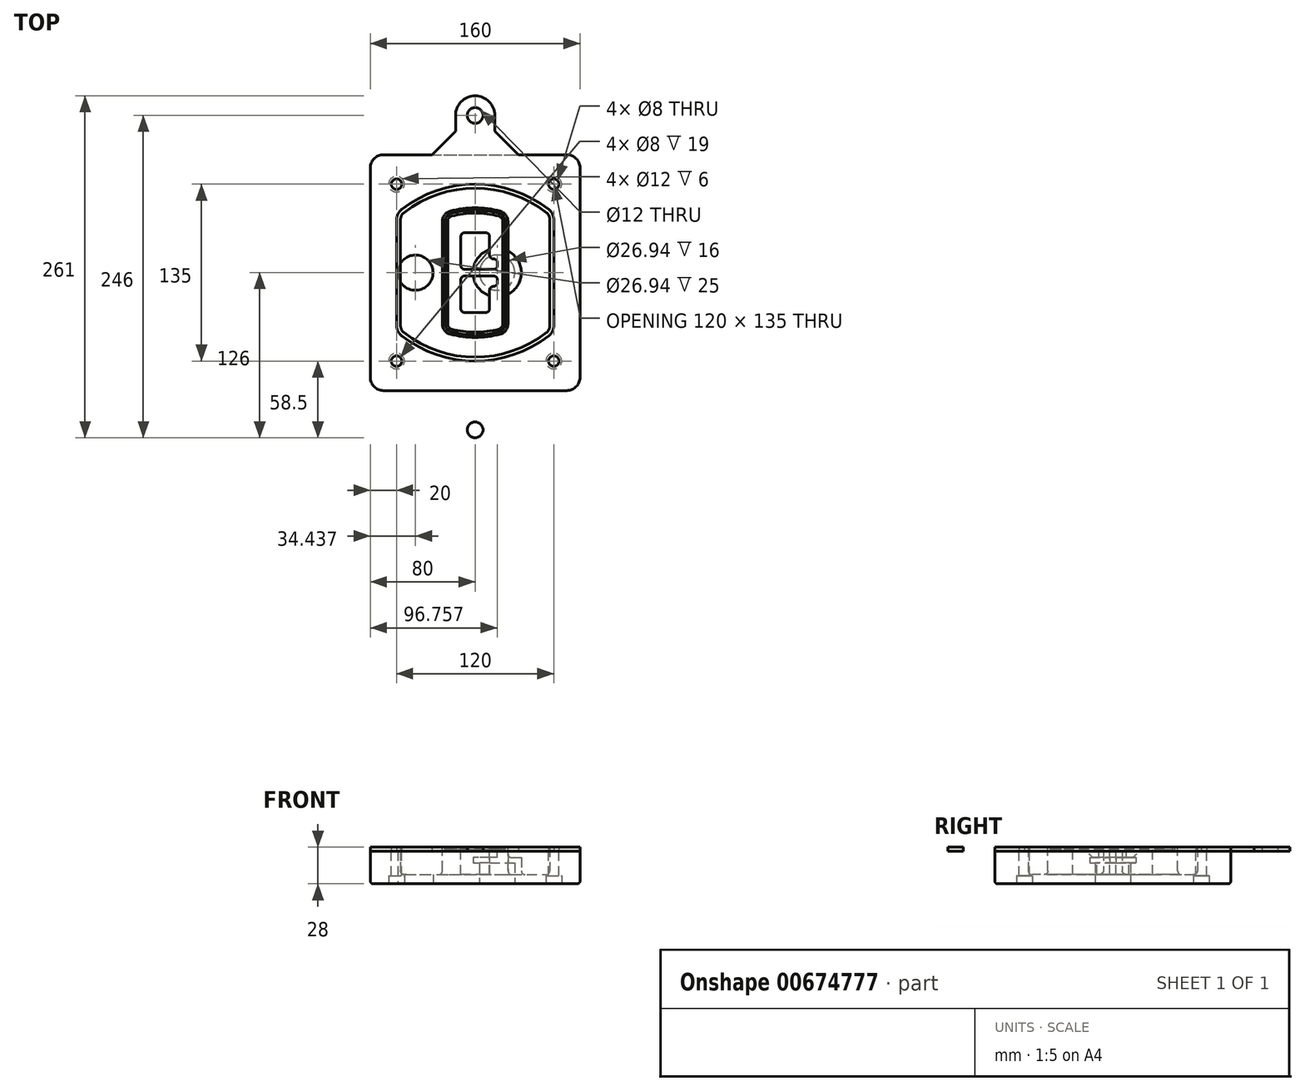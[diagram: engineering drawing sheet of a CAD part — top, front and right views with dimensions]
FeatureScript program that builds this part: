
annotation { "Feature Type Name" : "Feature", "Feature Type Description" : "" }
export const myFeature = defineFeature(function(context is Context, id is Id, definition is map)
    precondition{}
    {
        {
            var Q0;
            Q0=qCreatedBy(makeId("Top.planeOp"),FACE);
            var sketch = newSketch(context, id + "F0", { "sketchPlane" : qUnion([Q0])});
            skPoint(sketch, "E0.rect.middle", {"position": v(0, 0) * mm});
            skLineSegment(sketch, "E1.bottom", {"start": v(-70, -90) * mm, "end": v(70, -90) * mm});
            skLineSegment(sketch, "E1.top", {"start": v(-70, 90) * mm, "end": v(70, 90) * mm});
            skLineSegment(sketch, "E1.left", {"start": v(-80, -80) * mm, "end": v(-80, 80) * mm});
            skLineSegment(sketch, "E1.right", {"start": v(80, -80) * mm, "end": v(80, 80) * mm});
            skLineSegment(sketch, "E2", {"start": v(-80, 90) * mm, "end": v(80, -90) * mm, "construction": true});
            skLineSegment(sketch, "E3", {"start": v(80, 90) * mm, "end": v(-80, -90) * mm, "construction": true});
            skCircle(sketch, "E4", {"center": v(-60, 67.5) * mm, "radius": 4 * mm});
            skCircle(sketch, "E5", {"center": v(60, 67.5) * mm, "radius": 4 * mm});
            skCircle(sketch, "E6", {"center": v(60, -67.5) * mm, "radius": 4 * mm});
            skCircle(sketch, "E7", {"center": v(-60, -67.5) * mm, "radius": 4 * mm});
            skLineSegment(sketch, "E8", {"start": v(-60, 67.5) * mm, "end": v(60, 67.5) * mm, "construction": true});
            skLineSegment(sketch, "E9", {"start": v(60, 67.5) * mm, "end": v(60, -67.5) * mm, "construction": true});
            skLineSegment(sketch, "E10", {"start": v(60, -67.5) * mm, "end": v(-60, -67.5) * mm, "construction": true});
            skLineSegment(sketch, "E11", {"start": v(-60, -67.5) * mm, "end": v(-60, 67.5) * mm, "construction": true});
            skLineSegment(sketch, "E12", {"start": v(-60, 40.3) * mm, "end": v(-60, -40.3) * mm});
            skLineSegment(sketch, "E13", {"start": v(60, 40.3) * mm, "end": v(60, -40.3) * mm});
            skArc(sketch, "E14", {"start": v(56.15, 48.18) * mm, "mid": v(0, 67.5) * mm, "end": v(-56.15, 48.18) * mm});
            skArc(sketch, "E15", {"start": v(-56.15, -48.18) * mm, "mid": v(0, -67.5) * mm, "end": v(56.15, -48.18) * mm});
            skLineSegment(sketch, "E16", {"start": v(-60, 0) * mm, "end": v(60, 0) * mm, "construction": true});
            skPoint(sketch, "E17.visualSharp", {"position": v(-60, -45) * mm});
            skArc(sketch, "E17.filletArc", {"start": v(-60, -40.3) * mm, "mid": v(-58.99, -44.68) * mm, "end": v(-56.15, -48.18) * mm});
            skPoint(sketch, "E18.visualSharp", {"position": v(-60, 45) * mm});
            skArc(sketch, "E18.filletArc", {"start": v(-56.15, 48.18) * mm, "mid": v(-58.99, 44.68) * mm, "end": v(-60, 40.3) * mm});
            skPoint(sketch, "E19.visualSharp", {"position": v(60, 45) * mm});
            skArc(sketch, "E19.filletArc", {"start": v(60, 40.3) * mm, "mid": v(58.99, 44.68) * mm, "end": v(56.15, 48.18) * mm});
            skPoint(sketch, "E20.visualSharp", {"position": v(60, -45) * mm});
            skArc(sketch, "E20.filletArc", {"start": v(56.15, -48.18) * mm, "mid": v(58.99, -44.68) * mm, "end": v(60, -40.3) * mm});
            skPoint(sketch, "E21.visualSharp", {"position": v(-80, 90) * mm});
            skArc(sketch, "E21.filletArc", {"start": v(-70, 90) * mm, "mid": v(-77.07, 87.07) * mm, "end": v(-80, 80) * mm});
            skPoint(sketch, "E22.visualSharp", {"position": v(80, 90) * mm});
            skArc(sketch, "E22.filletArc", {"start": v(80, 80) * mm, "mid": v(77.07, 87.07) * mm, "end": v(70, 90) * mm});
            skPoint(sketch, "E23.visualSharp", {"position": v(80, -90) * mm});
            skArc(sketch, "E23.filletArc", {"start": v(70, -90) * mm, "mid": v(77.07, -87.07) * mm, "end": v(80, -80) * mm});
            skPoint(sketch, "E24.visualSharp", {"position": v(-80, -90) * mm});
            skArc(sketch, "E24.filletArc", {"start": v(-80, -80) * mm, "mid": v(-77.07, -87.07) * mm, "end": v(-70, -90) * mm});
            skArc(sketch, "E25.0", {"start": v(57, 40.3) * mm, "mid": v(56.3, 43.36) * mm, "end": v(54.3, 45.81) * mm});
            skLineSegment(sketch, "E25.1", {"start": v(57, 40.3) * mm, "end": v(57, -40.3) * mm});
            skArc(sketch, "E25.2", {"start": v(54.3, -45.81) * mm, "mid": v(56.3, -43.36) * mm, "end": v(57, -40.3) * mm});
            skArc(sketch, "E25.3", {"start": v(-54.3, -45.81) * mm, "mid": v(0, -64.5) * mm, "end": v(54.3, -45.81) * mm});
            skArc(sketch, "E25.4", {"start": v(-57, -40.3) * mm, "mid": v(-56.3, -43.36) * mm, "end": v(-54.3, -45.81) * mm});
            skArc(sketch, "E25.5", {"start": v(54.3, 45.81) * mm, "mid": v(0, 64.5) * mm, "end": v(-54.3, 45.81) * mm});
            skLineSegment(sketch, "E25.6", {"start": v(-57, 40.3) * mm, "end": v(-57, -40.3) * mm});
            skArc(sketch, "E25.7", {"start": v(-54.3, 45.81) * mm, "mid": v(-56.3, 43.36) * mm, "end": v(-57, 40.3) * mm});
            skArc(sketch, "E26.0", {"start": v(-58.62, 51.33) * mm, "mid": v(-62.58, 46.43) * mm, "end": v(-64, 40.3) * mm});
            skArc(sketch, "E26.1", {"start": v(58.62, 51.33) * mm, "mid": v(0, 71.5) * mm, "end": v(-58.62, 51.33) * mm});
            skArc(sketch, "E26.2", {"start": v(64, 40.3) * mm, "mid": v(62.58, 46.43) * mm, "end": v(58.62, 51.33) * mm});
            skLineSegment(sketch, "E26.3", {"start": v(64, 40.3) * mm, "end": v(64, -40.3) * mm});
            skArc(sketch, "E26.4", {"start": v(58.62, -51.33) * mm, "mid": v(62.58, -46.43) * mm, "end": v(64, -40.3) * mm});
            skLineSegment(sketch, "E26.5", {"start": v(-64, 40.3) * mm, "end": v(-64, -40.3) * mm});
            skArc(sketch, "E26.6", {"start": v(-58.62, -51.33) * mm, "mid": v(0, -71.5) * mm, "end": v(58.62, -51.33) * mm});
            skArc(sketch, "E26.7", {"start": v(-64, -40.3) * mm, "mid": v(-62.58, -46.43) * mm, "end": v(-58.62, -51.33) * mm});
            skSolve(sketch);
        }
        {
            var Q0;
            Q0=makeQuery(id+"F0.imprint","IMPRINT",FACE,{"disambiguationData":[TD([[makeQuery(id+"F0.imprint","IMPRINT",EDGE,{"derivedFrom":sQuery(id+"F0.wireOp",EDGE,"E1.bottom")}),1.0]])]});
            var Q1;
            Q1=makeQuery(id+"F0.imprint","IMPRINT",FACE,{"disambiguationData":[TD([[makeQuery(id+"F0.imprint","IMPRINT",EDGE,{"derivedFrom":sQuery(id+"F0.wireOp",EDGE,"E12")}),1.0]])]});
            var Q2;
            Q2=makeQuery(id+"F0.imprint","IMPRINT",FACE,{"disambiguationData":[TD([[makeQuery(id+"F0.imprint","IMPRINT",EDGE,{"derivedFrom":sQuery(id+"F0.wireOp",EDGE,"E25.0")}),1.0]])]});
            var Q3;
            Q3=makeQuery(id+"F0.imprint","IMPRINT",FACE,{"disambiguationData":[TD([[makeQuery(id+"F0.imprint","IMPRINT",EDGE,{"derivedFrom":sQuery(id+"F0.wireOp",EDGE,"E12")}),-1.0]])]});
            extrude(context, id + "F1", {"entities" : qUnion([Q0, Q1, Q2, Q3]), "oppositeDirection" : true, "depth" : 25 * mm});
        }
        {
            var Q0;
            Q0=makeQuery(id+"F0.imprint","IMPRINT",FACE,{"disambiguationData":[TD([[makeQuery(id+"F0.imprint","IMPRINT",EDGE,{"derivedFrom":sQuery(id+"F0.wireOp",EDGE,"E12")}),1.0]])]});
            extrude(context, id + "F2", {"entities" : qUnion([Q0]), "operationType" : NewBodyOperationType.ADD, "depth" : 3 * mm});
        }
        {
            var Q0;
            Q0=makeQuery(id+"F0.imprint","IMPRINT",FACE,{"disambiguationData":[TD([[makeQuery(id+"F0.imprint","IMPRINT",EDGE,{"derivedFrom":sQuery(id+"F0.wireOp",EDGE,"E25.0")}),1.0]])]});
            extrude(context, id + "F3", {"entities" : qUnion([Q0]), "operationType" : NewBodyOperationType.REMOVE, "oppositeDirection" : true, "depth" : 18 * mm});
        }
        {
            var Q0;
            Q0=makeQuery(id+"F2.opExtrude","CAP_FACE",FACE,{"disambiguationData":[OSD([sQuery(id+"F0.wireOp",EDGE,"E12"),sQuery(id+"F0.wireOp",EDGE,"E13"),sQuery(id+"F0.wireOp",EDGE,"E14"),sQuery(id+"F0.wireOp",EDGE,"E15"),sQuery(id+"F0.wireOp",EDGE,"E17.filletArc"),sQuery(id+"F0.wireOp",EDGE,"E18.filletArc"),sQuery(id+"F0.wireOp",EDGE,"E19.filletArc"),sQuery(id+"F0.wireOp",EDGE,"E20.filletArc"),sQuery(id+"F0.wireOp",EDGE,"E25.0"),sQuery(id+"F0.wireOp",EDGE,"E25.1"),sQuery(id+"F0.wireOp",EDGE,"E25.2"),sQuery(id+"F0.wireOp",EDGE,"E25.3"),sQuery(id+"F0.wireOp",EDGE,"E25.4"),sQuery(id+"F0.wireOp",EDGE,"E25.5"),sQuery(id+"F0.wireOp",EDGE,"E25.6"),sQuery(id+"F0.wireOp",EDGE,"E25.7")])],"isStart":false});
            var sketch = newSketch(context, id + "F4", { "sketchPlane" : qUnion([Q0])});
            skArc(sketch, "E27.0", {"start": v(-19.08, -46.97) * mm, "mid": v(0, -49.5) * mm, "end": v(19.08, -46.97) * mm});
            skArc(sketch, "E28.0", {"start": v(19.08, 46.97) * mm, "mid": v(0, 49.5) * mm, "end": v(-19.08, 46.97) * mm});
            skLineSegment(sketch, "E29", {"start": v(-25, 39.25) * mm, "end": v(-25, -39.25) * mm});
            skLineSegment(sketch, "E30", {"start": v(25, 39.25) * mm, "end": v(25, -39.25) * mm});
            skLineSegment(sketch, "E31", {"start": v(-25, 45.1) * mm, "end": v(25, 45.1) * mm, "construction": true});
            skLineSegment(sketch, "E32", {"start": v(-25, -45.1) * mm, "end": v(25, -45.1) * mm, "construction": true});
            skPoint(sketch, "E33.visualSharp", {"position": v(-25, 45.1) * mm});
            skArc(sketch, "E33.filletArc", {"start": v(-19.08, 46.97) * mm, "mid": v(-23.35, 44.11) * mm, "end": v(-25, 39.25) * mm});
            skPoint(sketch, "E34.visualSharp", {"position": v(25, 45.1) * mm});
            skArc(sketch, "E34.filletArc", {"start": v(25, 39.25) * mm, "mid": v(23.35, 44.11) * mm, "end": v(19.08, 46.97) * mm});
            skPoint(sketch, "E35.visualSharp", {"position": v(25, -45.1) * mm});
            skArc(sketch, "E35.filletArc", {"start": v(19.08, -46.97) * mm, "mid": v(23.35, -44.11) * mm, "end": v(25, -39.25) * mm});
            skPoint(sketch, "E36.visualSharp", {"position": v(-25, -45.1) * mm});
            skArc(sketch, "E36.filletArc", {"start": v(-25, -39.25) * mm, "mid": v(-23.35, -44.11) * mm, "end": v(-19.08, -46.97) * mm});
            skArc(sketch, "E37.0", {"start": v(54.3, 45.81) * mm, "mid": v(0, 64.5) * mm, "end": v(-54.3, 45.81) * mm});
            skArc(sketch, "E37.1", {"start": v(-54.3, 45.81) * mm, "mid": v(-56.3, 43.36) * mm, "end": v(-57, 40.3) * mm});
            skLineSegment(sketch, "E37.2", {"start": v(-57, 40.3) * mm, "end": v(-57, -40.3) * mm});
            skArc(sketch, "E37.3", {"start": v(-57, -40.3) * mm, "mid": v(-56.3, -43.36) * mm, "end": v(-54.3, -45.81) * mm});
            skArc(sketch, "E37.4", {"start": v(-54.3, -45.81) * mm, "mid": v(0, -64.5) * mm, "end": v(54.3, -45.81) * mm});
            skArc(sketch, "E37.5", {"start": v(54.3, -45.81) * mm, "mid": v(56.3, -43.36) * mm, "end": v(57, -40.3) * mm});
            skLineSegment(sketch, "E37.6", {"start": v(57, 40.3) * mm, "end": v(57, -40.3) * mm});
            skArc(sketch, "E37.7", {"start": v(57, 40.3) * mm, "mid": v(56.3, 43.36) * mm, "end": v(54.3, 45.81) * mm});
            skLineSegment(sketch, "E38.0", {"start": v(23, 39.25) * mm, "end": v(23, -39.25) * mm});
            skArc(sketch, "E38.1", {"start": v(18.56, -45.04) * mm, "mid": v(21.76, -42.9) * mm, "end": v(23, -39.25) * mm});
            skArc(sketch, "E38.2", {"start": v(-18.56, -45.04) * mm, "mid": v(0, -47.5) * mm, "end": v(18.56, -45.04) * mm});
            skArc(sketch, "E38.3", {"start": v(-23, -39.25) * mm, "mid": v(-21.76, -42.9) * mm, "end": v(-18.56, -45.04) * mm});
            skLineSegment(sketch, "E38.4", {"start": v(-23, 39.25) * mm, "end": v(-23, -39.25) * mm});
            skArc(sketch, "E38.5", {"start": v(23, 39.25) * mm, "mid": v(21.76, 42.9) * mm, "end": v(18.56, 45.04) * mm});
            skArc(sketch, "E38.6", {"start": v(-18.56, 45.04) * mm, "mid": v(-21.76, 42.9) * mm, "end": v(-23, 39.25) * mm});
            skArc(sketch, "E38.7", {"start": v(18.56, 45.04) * mm, "mid": v(0, 47.5) * mm, "end": v(-18.56, 45.04) * mm});
            skArc(sketch, "E39.0", {"start": v(21, 39.25) * mm, "mid": v(20.18, 41.68) * mm, "end": v(18.04, 43.1) * mm});
            skLineSegment(sketch, "E39.1", {"start": v(21, 39.25) * mm, "end": v(21, -39.25) * mm});
            skArc(sketch, "E39.2", {"start": v(18.04, -43.1) * mm, "mid": v(20.18, -41.68) * mm, "end": v(21, -39.25) * mm});
            skArc(sketch, "E39.3", {"start": v(-18.04, -43.1) * mm, "mid": v(0, -45.5) * mm, "end": v(18.04, -43.1) * mm});
            skArc(sketch, "E39.4", {"start": v(-21, -39.25) * mm, "mid": v(-20.18, -41.68) * mm, "end": v(-18.04, -43.1) * mm});
            skArc(sketch, "E39.5", {"start": v(18.04, 43.1) * mm, "mid": v(0, 45.5) * mm, "end": v(-18.04, 43.1) * mm});
            skLineSegment(sketch, "E39.6", {"start": v(-21, 39.25) * mm, "end": v(-21, -39.25) * mm});
            skArc(sketch, "E39.7", {"start": v(-18.04, 43.1) * mm, "mid": v(-20.18, 41.68) * mm, "end": v(-21, 39.25) * mm});
            skLineSegment(sketch, "E40", {"start": v(-25, 0) * mm, "end": v(25, 0) * mm, "construction": true});
            skLineSegment(sketch, "E41", {"start": v(-11, 5.5) * mm, "end": v(-11, 27.5) * mm});
            skLineSegment(sketch, "E42", {"start": v(-8, 30.5) * mm, "end": v(8, 30.5) * mm});
            skLineSegment(sketch, "E43", {"start": v(11, 27.5) * mm, "end": v(11, 13.5) * mm});
            skLineSegment(sketch, "E44", {"start": v(14, 10.5) * mm, "end": v(14, 10.5) * mm});
            skLineSegment(sketch, "E45", {"start": v(17, 7.5) * mm, "end": v(17, 5.5) * mm});
            skLineSegment(sketch, "E46", {"start": v(14, 2.5) * mm, "end": v(-8, 2.5) * mm});
            skPoint(sketch, "E47.visualSharp", {"position": v(-11, 30.5) * mm});
            skArc(sketch, "E47.filletArc", {"start": v(-8, 30.5) * mm, "mid": v(-10.12, 29.62) * mm, "end": v(-11, 27.5) * mm});
            skPoint(sketch, "E48.visualSharp", {"position": v(11, 30.5) * mm});
            skArc(sketch, "E48.filletArc", {"start": v(11, 27.5) * mm, "mid": v(10.12, 29.62) * mm, "end": v(8, 30.5) * mm});
            skPoint(sketch, "E49.visualSharp", {"position": v(11, 10.5) * mm});
            skArc(sketch, "E49.filletArc", {"start": v(11, 13.5) * mm, "mid": v(11.88, 11.38) * mm, "end": v(14, 10.5) * mm});
            skPoint(sketch, "E50.visualSharp", {"position": v(17, 10.5) * mm});
            skArc(sketch, "E50.filletArc", {"start": v(17, 7.5) * mm, "mid": v(16.12, 9.62) * mm, "end": v(14, 10.5) * mm});
            skPoint(sketch, "E51.visualSharp", {"position": v(17, 2.5) * mm});
            skArc(sketch, "E51.filletArc", {"start": v(14, 2.5) * mm, "mid": v(16.12, 3.38) * mm, "end": v(17, 5.5) * mm});
            skPoint(sketch, "E52.visualSharp", {"position": v(-11, 2.5) * mm});
            skArc(sketch, "E52.filletArc", {"start": v(-11, 5.5) * mm, "mid": v(-10.12, 3.38) * mm, "end": v(-8, 2.5) * mm});
            skLineSegment(sketch, "E53.0.MirrorCS", {"start": v(14, -2.5) * mm, "end": v(-8, -2.5) * mm});
            skArc(sketch, "E54.0.MirrorCS", {"start": v(-11, -5.5) * mm, "mid": v(-10.12, -3.38) * mm, "end": v(-8, -2.5) * mm});
            skLineSegment(sketch, "E55.0.MirrorCS", {"start": v(-11, -5.5) * mm, "end": v(-11, -27.5) * mm});
            skArc(sketch, "E56.0.MirrorCS", {"start": v(-8, -30.5) * mm, "mid": v(-10.12, -29.62) * mm, "end": v(-11, -27.5) * mm});
            skLineSegment(sketch, "E57.0.MirrorCS", {"start": v(-8, -30.5) * mm, "end": v(8, -30.5) * mm});
            skArc(sketch, "E58.0.MirrorCS", {"start": v(11, -27.5) * mm, "mid": v(10.12, -29.62) * mm, "end": v(8, -30.5) * mm});
            skLineSegment(sketch, "E59.0.MirrorCS", {"start": v(11, -27.5) * mm, "end": v(11, -13.5) * mm});
            skArc(sketch, "E60.0.MirrorCS", {"start": v(11, -13.5) * mm, "mid": v(11.88, -11.38) * mm, "end": v(14, -10.5) * mm});
            skArc(sketch, "E61.0.MirrorCS", {"start": v(17, -7.5) * mm, "mid": v(16.12, -9.62) * mm, "end": v(14, -10.5) * mm});
            skLineSegment(sketch, "E62.0.MirrorCS", {"start": v(17, -7.5) * mm, "end": v(17, -5.5) * mm});
            skArc(sketch, "E63.0.MirrorCS", {"start": v(14, -2.5) * mm, "mid": v(16.12, -3.38) * mm, "end": v(17, -5.5) * mm});
            skSolve(sketch);
        }
        {
            var Q0;
            Q0=makeQuery(id+"F4.imprint","IMPRINT",FACE,{"disambiguationData":[TD([[makeQuery(id+"F4.imprint","IMPRINT",EDGE,{"derivedFrom":sQuery(id+"F4.wireOp",EDGE,"E27.0")}),1.0]])]});
            var Q1;
            Q1=makeQuery(id+"F4.imprint","IMPRINT",FACE,{"disambiguationData":[TD([[makeQuery(id+"F4.imprint","IMPRINT",EDGE,{"derivedFrom":sQuery(id+"F4.wireOp",EDGE,"E38.0")}),-1.0]])]});
            var Q2;
            Q2=makeQuery(id+"F4.imprint","IMPRINT",FACE,{"disambiguationData":[TD([[makeQuery(id+"F4.imprint","IMPRINT",EDGE,{"derivedFrom":sQuery(id+"F4.wireOp",EDGE,"E39.0")}),1.0]])]});
            extrude(context, id + "F5", {"entities" : qUnion([Q0, Q1, Q2]), "operationType" : NewBodyOperationType.ADD, "endBound" : BoundingType.UP_TO_NEXT, "oppositeDirection" : true, "depth" : 25 * mm});
        }
        {
            var Q0;
            Q0=makeQuery(id+"F4.imprint","IMPRINT",FACE,{"disambiguationData":[TD([[makeQuery(id+"F4.imprint","IMPRINT",EDGE,{"derivedFrom":sQuery(id+"F4.wireOp",EDGE,"E38.0")}),-1.0]])]});
            extrude(context, id + "F6", {"entities" : qUnion([Q0]), "operationType" : NewBodyOperationType.REMOVE, "oppositeDirection" : true, "depth" : 2 * mm});
        }
        {
            var Q0;
            Q0=makeQuery(id+"F1.opExtrude","CAP_FACE",FACE,{"disambiguationData":[OSD([sQuery(id+"F0.wireOp",EDGE,"E1.bottom"),sQuery(id+"F0.wireOp",EDGE,"E1.top"),sQuery(id+"F0.wireOp",EDGE,"E1.left"),sQuery(id+"F0.wireOp",EDGE,"E1.right"),sQuery(id+"F0.wireOp",EDGE,"E4"),sQuery(id+"F0.wireOp",EDGE,"E5"),sQuery(id+"F0.wireOp",EDGE,"E6"),sQuery(id+"F0.wireOp",EDGE,"E7"),sQuery(id+"F0.wireOp",EDGE,"E21.filletArc"),sQuery(id+"F0.wireOp",EDGE,"E22.filletArc"),sQuery(id+"F0.wireOp",EDGE,"E23.filletArc"),sQuery(id+"F0.wireOp",EDGE,"E24.filletArc")])],"isStart":false});
            var sketch = newSketch(context, id + "F7", { "sketchPlane" : qUnion([Q0])});
            skCircle(sketch, "E64", {"center": v(16.76, 0) * mm, "radius": 13.47 * mm});
            skCircle(sketch, "E65", {"center": v(-45.56, 0) * mm, "radius": 13.47 * mm});
            skLineSegment(sketch, "E66", {"start": v(80, 0) * mm, "end": v(-80, 0) * mm});
            skCircle(sketch, "E67", {"center": v(16.76, 0) * mm, "radius": 18.47 * mm});
            skCircle(sketch, "E68", {"center": v(60, -67.5) * mm, "radius": 6 * mm});
            skCircle(sketch, "E69", {"center": v(-60, -67.5) * mm, "radius": 6 * mm});
            skCircle(sketch, "E70", {"center": v(-60, 67.5) * mm, "radius": 6 * mm});
            skCircle(sketch, "E71", {"center": v(60, 67.5) * mm, "radius": 6 * mm});
            skSolve(sketch);
        }
        {
            var Q0;
            {var subQ1=sQuery(id+"F7.wireOp",EDGE,"E66");var subQ4=sQuery(id+"F7.wireOp",EDGE,"E64");var subQ6=makeQuery(id+"F7.imprint","INTERSECT",VERTEX,{"disambiguationData":[OD(0.0)],"derivedFrom":[subQ4,subQ1]});Q0=makeQuery(id+"F7.imprint","IMPRINT",FACE,{"disambiguationData":[TD([[makeQuery(id+"F7.imprint","IMPRINT",EDGE,{"disambiguationData":[TD([[subQ6,-1.0]])],"derivedFrom":subQ4}),-1.0]])]});}
            var Q1;
            {var subQ0=sQuery(id+"F7.wireOp",EDGE,"E66");var subQ1=sQuery(id+"F7.wireOp",EDGE,"E64");var subQ3=makeQuery(id+"F7.imprint","INTERSECT",VERTEX,{"disambiguationData":[OD(0.0)],"derivedFrom":[subQ1,subQ0]});Q1=makeQuery(id+"F7.imprint","IMPRINT",FACE,{"disambiguationData":[TD([[makeQuery(id+"F7.imprint","IMPRINT",EDGE,{"disambiguationData":[TD([[subQ3,-1.0]])],"derivedFrom":subQ1}),1.0]])]});}
            var Q2;
            {var subQ0=sQuery(id+"F7.wireOp",EDGE,"E66");var subQ1=sQuery(id+"F7.wireOp",EDGE,"E64");var subQ3=makeQuery(id+"F7.imprint","INTERSECT",VERTEX,{"disambiguationData":[OD(0.0)],"derivedFrom":[subQ1,subQ0]});Q2=makeQuery(id+"F7.imprint","IMPRINT",FACE,{"disambiguationData":[TD([[makeQuery(id+"F7.imprint","IMPRINT",EDGE,{"disambiguationData":[TD([[subQ3,1.0]])],"derivedFrom":subQ1}),1.0]])]});}
            var Q3;
            {var subQ1=sQuery(id+"F7.wireOp",EDGE,"E66");var subQ4=sQuery(id+"F7.wireOp",EDGE,"E64");var subQ6=makeQuery(id+"F7.imprint","INTERSECT",VERTEX,{"disambiguationData":[OD(0.0)],"derivedFrom":[subQ4,subQ1]});Q3=makeQuery(id+"F7.imprint","IMPRINT",FACE,{"disambiguationData":[TD([[makeQuery(id+"F7.imprint","IMPRINT",EDGE,{"disambiguationData":[TD([[subQ6,1.0]])],"derivedFrom":subQ4}),-1.0]])]});}
            extrude(context, id + "F8", {"entities" : qUnion([Q0, Q1, Q2, Q3]), "operationType" : NewBodyOperationType.ADD, "oppositeDirection" : true, "depth" : 20 * mm});
        }
        {
            var Q0;
            {var subQ0=sQuery(id+"F7.wireOp",EDGE,"E66");var subQ1=sQuery(id+"F7.wireOp",EDGE,"E64");var subQ3=makeQuery(id+"F7.imprint","INTERSECT",VERTEX,{"disambiguationData":[OD(0.0)],"derivedFrom":[subQ1,subQ0]});Q0=makeQuery(id+"F7.imprint","IMPRINT",FACE,{"disambiguationData":[TD([[makeQuery(id+"F7.imprint","IMPRINT",EDGE,{"disambiguationData":[TD([[subQ3,-1.0]])],"derivedFrom":subQ1}),1.0]])]});}
            var Q1;
            {var subQ0=sQuery(id+"F7.wireOp",EDGE,"E66");var subQ1=sQuery(id+"F7.wireOp",EDGE,"E64");var subQ3=makeQuery(id+"F7.imprint","INTERSECT",VERTEX,{"disambiguationData":[OD(0.0)],"derivedFrom":[subQ1,subQ0]});Q1=makeQuery(id+"F7.imprint","IMPRINT",FACE,{"disambiguationData":[TD([[makeQuery(id+"F7.imprint","IMPRINT",EDGE,{"disambiguationData":[TD([[subQ3,1.0]])],"derivedFrom":subQ1}),1.0]])]});}
            extrude(context, id + "F9", {"entities" : qUnion([Q0, Q1]), "operationType" : NewBodyOperationType.REMOVE, "oppositeDirection" : true, "depth" : 16 * mm});
        }
        {
            var Q0;
            {var subQ0=sQuery(id+"F7.wireOp",EDGE,"E66");var subQ1=sQuery(id+"F7.wireOp",EDGE,"E65");var subQ3=makeQuery(id+"F7.imprint","INTERSECT",VERTEX,{"disambiguationData":[OD(0.0)],"derivedFrom":[subQ1,subQ0]});Q0=makeQuery(id+"F7.imprint","IMPRINT",FACE,{"disambiguationData":[TD([[makeQuery(id+"F7.imprint","IMPRINT",EDGE,{"disambiguationData":[TD([[subQ3,-1.0]])],"derivedFrom":subQ1}),1.0]])]});}
            var Q1;
            {var subQ0=sQuery(id+"F7.wireOp",EDGE,"E66");var subQ1=sQuery(id+"F7.wireOp",EDGE,"E65");var subQ3=makeQuery(id+"F7.imprint","INTERSECT",VERTEX,{"disambiguationData":[OD(0.0)],"derivedFrom":[subQ1,subQ0]});Q1=makeQuery(id+"F7.imprint","IMPRINT",FACE,{"disambiguationData":[TD([[makeQuery(id+"F7.imprint","IMPRINT",EDGE,{"disambiguationData":[TD([[subQ3,1.0]])],"derivedFrom":subQ1}),1.0]])]});}
            extrude(context, id + "F10", {"entities" : qUnion([Q0, Q1]), "operationType" : NewBodyOperationType.REMOVE, "oppositeDirection" : true, "depth" : 25 * mm});
        }
        {
            var Q0;
            Q0=makeQuery(id+"F7.imprint","IMPRINT",FACE,{"disambiguationData":[TD([[makeQuery(id+"F7.imprint","IMPRINT",EDGE,{"derivedFrom":sQuery(id+"F7.wireOp",EDGE,"E68")}),1.0]])]});
            var Q1;
            Q1=makeQuery(id+"F7.imprint","IMPRINT",FACE,{"disambiguationData":[TD([[makeQuery(id+"F7.imprint","IMPRINT",EDGE,{"derivedFrom":makeQuery(id+"F1.opExtrude","CAP_EDGE",EDGE,{"disambiguationData":[OSD([sQuery(id+"F0.wireOp",EDGE,"E5")])],"isStart":false})}),-1.0]])]});
            var Q2;
            Q2=makeQuery(id+"F7.imprint","IMPRINT",FACE,{"disambiguationData":[TD([[makeQuery(id+"F7.imprint","IMPRINT",EDGE,{"derivedFrom":sQuery(id+"F7.wireOp",EDGE,"E69")}),1.0]])]});
            var Q3;
            Q3=makeQuery(id+"F7.imprint","IMPRINT",FACE,{"disambiguationData":[TD([[makeQuery(id+"F7.imprint","IMPRINT",EDGE,{"derivedFrom":makeQuery(id+"F1.opExtrude","CAP_EDGE",EDGE,{"disambiguationData":[OSD([sQuery(id+"F0.wireOp",EDGE,"E4")])],"isStart":false})}),-1.0]])]});
            var Q4;
            Q4=makeQuery(id+"F7.imprint","IMPRINT",FACE,{"disambiguationData":[TD([[makeQuery(id+"F7.imprint","IMPRINT",EDGE,{"derivedFrom":sQuery(id+"F7.wireOp",EDGE,"E70")}),1.0]])]});
            var Q5;
            Q5=makeQuery(id+"F7.imprint","IMPRINT",FACE,{"disambiguationData":[TD([[makeQuery(id+"F7.imprint","IMPRINT",EDGE,{"derivedFrom":makeQuery(id+"F1.opExtrude","CAP_EDGE",EDGE,{"disambiguationData":[OSD([sQuery(id+"F0.wireOp",EDGE,"E7")])],"isStart":false})}),-1.0]])]});
            var Q6;
            Q6=makeQuery(id+"F7.imprint","IMPRINT",FACE,{"disambiguationData":[TD([[makeQuery(id+"F7.imprint","IMPRINT",EDGE,{"derivedFrom":sQuery(id+"F7.wireOp",EDGE,"E71")}),1.0]])]});
            var Q7;
            Q7=makeQuery(id+"F7.imprint","IMPRINT",FACE,{"disambiguationData":[TD([[makeQuery(id+"F7.imprint","IMPRINT",EDGE,{"derivedFrom":makeQuery(id+"F1.opExtrude","CAP_EDGE",EDGE,{"disambiguationData":[OSD([sQuery(id+"F0.wireOp",EDGE,"E6")])],"isStart":false})}),-1.0]])]});
            extrude(context, id + "F11", {"entities" : qUnion([Q0, Q1, Q2, Q3, Q4, Q5, Q6, Q7]), "operationType" : NewBodyOperationType.REMOVE, "oppositeDirection" : true, "depth" : 6 * mm});
        }
        {
            var Q0;
            Q0=makeQuery(id+"F9.boolean.opBoolean","COPY",FACE,{"derivedFrom":makeQuery(id+"F9.opExtrude","CAP_FACE",FACE,{"disambiguationData":[OSD([sQuery(id+"F7.wireOp",EDGE,"E64")])],"isStart":false})});
            var sketch = newSketch(context, id + "F12", { "sketchPlane" : qUnion([Q0])});
            skArc(sketch, "E72.0", {"start": v(11, 17.55) * mm, "mid": v(2.57, 11.82) * mm, "end": v(-1.54, 2.5) * mm});
            skArc(sketch, "E72.1", {"start": v(-1.54, -2.5) * mm, "mid": v(2.57, -11.82) * mm, "end": v(11, -17.55) * mm});
            skLineSegment(sketch, "E73", {"start": v(-1.54, -2.5) * mm, "end": v(14, -2.5) * mm});
            skLineSegment(sketch, "E74.0", {"start": v(14, 2.5) * mm, "end": v(-1.54, 2.5) * mm});
            skArc(sketch, "E74.1", {"start": v(14, 2.5) * mm, "mid": v(16.12, 3.38) * mm, "end": v(17, 5.5) * mm});
            skLineSegment(sketch, "E74.2", {"start": v(17, 7.5) * mm, "end": v(17, 5.5) * mm});
            skArc(sketch, "E74.3", {"start": v(17, 7.5) * mm, "mid": v(16.12, 9.62) * mm, "end": v(14, 10.5) * mm});
            skArc(sketch, "E74.4", {"start": v(11, 13.5) * mm, "mid": v(11.88, 11.38) * mm, "end": v(14, 10.5) * mm});
            skLineSegment(sketch, "E74.5", {"start": v(11, 17.55) * mm, "end": v(11, 13.5) * mm});
            skLineSegment(sketch, "E74.7", {"start": v(14, -2.5) * mm, "end": v(-1.54, -2.5) * mm});
            skArc(sketch, "E74.8", {"start": v(14, -2.5) * mm, "mid": v(16.12, -3.38) * mm, "end": v(17, -5.5) * mm});
            skLineSegment(sketch, "E74.9", {"start": v(17, -7.5) * mm, "end": v(17, -5.5) * mm});
            skArc(sketch, "E74.10", {"start": v(17, -7.5) * mm, "mid": v(16.12, -9.62) * mm, "end": v(14, -10.5) * mm});
            skArc(sketch, "E74.11", {"start": v(11, -13.5) * mm, "mid": v(11.88, -11.38) * mm, "end": v(14, -10.5) * mm});
            skLineSegment(sketch, "E74.12", {"start": v(11, -17.55) * mm, "end": v(11, -13.5) * mm});
            skPoint(sketch, "E75.orphan", {"position": v(11, -27.5) * mm});
            skPoint(sketch, "E76.orphan", {"position": v(-8, -2.5) * mm});
            skPoint(sketch, "E77.orphan", {"position": v(-8, 2.5) * mm});
            skPoint(sketch, "E78.orphan", {"position": v(11, 27.5) * mm});
            skSolve(sketch);
        }
        {
            var Q0;
            {var subQ7=sQuery(id+"F12.wireOp",EDGE,"E72.0");var subQ14=sQuery(id+"F12.wireOp",EDGE,"E72.1");var subQ16=sQuery(id+"F12.wireOp",EDGE,"E74.1");var subQ18=sQuery(id+"F12.wireOp",EDGE,"E74.8");Q0=qUnion([makeQuery(id+"F12.imprint","IMPRINT",FACE,{"disambiguationData":[TD([[makeQuery(id+"F12.imprint","IMPRINT",EDGE,{"derivedFrom":subQ7}),1.0]])]}),makeQuery(id+"F12.imprint","IMPRINT",FACE,{"disambiguationData":[TD([[makeQuery(id+"F12.imprint","IMPRINT",EDGE,{"derivedFrom":subQ14}),1.0]])]}),makeQuery(id+"F12.imprint","IMPRINT",FACE,{"disambiguationData":[TD([[makeQuery(id+"F12.imprint","IMPRINT",EDGE,{"derivedFrom":subQ16}),1.0]])]}),makeQuery(id+"F12.imprint","IMPRINT",FACE,{"disambiguationData":[TD([[makeQuery(id+"F12.imprint","IMPRINT",EDGE,{"derivedFrom":subQ18}),-1.0]])]})]);}
            var Q1;
            Q1=makeQuery(id+"F5.boolean.opBoolean","SPLIT",FACE,{"disambiguationData":[TD([makeQuery(id+"F5.opExtrude","SWEPT_FACE",FACE,{"disambiguationData":[OSD([sQuery(id+"F4.wireOp",EDGE,"E41")])]})])],"derivedFrom":makeQuery(id+"F3.boolean.opBoolean","COPY",FACE,{"derivedFrom":makeQuery(id+"F3.opExtrude","CAP_FACE",FACE,{"disambiguationData":[OSD([sQuery(id+"F0.wireOp",EDGE,"E25.0"),sQuery(id+"F0.wireOp",EDGE,"E25.1"),sQuery(id+"F0.wireOp",EDGE,"E25.2"),sQuery(id+"F0.wireOp",EDGE,"E25.3"),sQuery(id+"F0.wireOp",EDGE,"E25.4"),sQuery(id+"F0.wireOp",EDGE,"E25.5"),sQuery(id+"F0.wireOp",EDGE,"E25.6"),sQuery(id+"F0.wireOp",EDGE,"E25.7")])],"isStart":false})})});
            extrude(context, id + "F13", {"entities" : qUnion([Q0]), "operationType" : NewBodyOperationType.REMOVE, "endBound" : BoundingType.UP_TO_SURFACE, "endBoundEntityFace" : qUnion([Q1]), "depth" : 25 * mm});
        }
        {
            var Q0;
            Q0=makeQuery(id+"F3.boolean.opBoolean","COPY",EDGE,{"derivedFrom":makeQuery(id+"F3.opExtrude","CAP_EDGE",EDGE,{"disambiguationData":[OSD([sQuery(id+"F0.wireOp",EDGE,"E25.6")])],"isStart":false})});
            var Q1;
            Q1=makeQuery(id+"F8.boolean.opBoolean","INTERSECT",EDGE,{"derivedFrom":[makeQuery(id+"F5.opExtrude","SWEPT_FACE",FACE,{"disambiguationData":[OSD([sQuery(id+"F4.wireOp",EDGE,"E30")])]}),makeQuery(id+"F8.opExtrude","CAP_FACE",FACE,{"disambiguationData":[OSD([sQuery(id+"F7.wireOp",EDGE,"E67")])],"isStart":false})]});
            var Q2;
            Q2=makeQuery(id+"F8.boolean.opBoolean","INTERSECT",EDGE,{"disambiguationData":[OD(1.0)],"derivedFrom":[makeQuery(id+"F5.opExtrude","SWEPT_FACE",FACE,{"disambiguationData":[OSD([sQuery(id+"F4.wireOp",EDGE,"E30")])]}),makeQuery(id+"F8.opExtrude","SWEPT_FACE",FACE,{"disambiguationData":[OSD([sQuery(id+"F7.wireOp",EDGE,"E67")])]})]});
            var Q3;
            {var subQ0=sQuery(id+"F4.wireOp",EDGE,"E30");Q3=makeQuery(id+"F8.boolean.opBoolean","SPLIT",EDGE,{"disambiguationData":[TD([makeQuery(id+"F5.opExtrude","SWEPT_FACE",FACE,{"disambiguationData":[OSD([sQuery(id+"F4.wireOp",EDGE,"E35.filletArc")])]})])],"derivedFrom":makeQuery(id+"F5.opExtrude","CAP_EDGE",EDGE,{"disambiguationData":[OSD([subQ0])],"isStart":false})});}
            var Q4;
            {var subQ0=sQuery(id+"F0.wireOp",EDGE,"E25.7");var subQ1=sQuery(id+"F0.wireOp",EDGE,"E25.1");var subQ2=sQuery(id+"F0.wireOp",EDGE,"E25.6");var subQ3=sQuery(id+"F0.wireOp",EDGE,"E25.5");var subQ4=sQuery(id+"F0.wireOp",EDGE,"E25.4");var subQ5=sQuery(id+"F0.wireOp",EDGE,"E25.0");var subQ6=sQuery(id+"F0.wireOp",EDGE,"E25.2");var subQ7=sQuery(id+"F0.wireOp",EDGE,"E25.3");Q4=makeQuery(id+"F8.boolean.opBoolean","INTERSECT",EDGE,{"derivedFrom":[makeQuery(id+"F5.boolean.opBoolean","SPLIT",FACE,{"disambiguationData":[TD([makeQuery(id+"F2.opExtrude","SWEPT_FACE",FACE,{"disambiguationData":[OSD([subQ5])]})])],"derivedFrom":makeQuery(id+"F3.boolean.opBoolean","COPY",FACE,{"derivedFrom":makeQuery(id+"F3.opExtrude","CAP_FACE",FACE,{"disambiguationData":[OSD([subQ5,subQ1,subQ6,subQ7,subQ4,subQ3,subQ2,subQ0])],"isStart":false})})}),makeQuery(id+"F8.opExtrude","SWEPT_FACE",FACE,{"disambiguationData":[OSD([sQuery(id+"F7.wireOp",EDGE,"E67")])]})]});}
            var Q5;
            Q5=makeQuery(id+"F8.boolean.opBoolean","INTERSECT",EDGE,{"disambiguationData":[OD(0.0)],"derivedFrom":[makeQuery(id+"F5.opExtrude","SWEPT_FACE",FACE,{"disambiguationData":[OSD([sQuery(id+"F4.wireOp",EDGE,"E30")])]}),makeQuery(id+"F8.opExtrude","SWEPT_FACE",FACE,{"disambiguationData":[OSD([sQuery(id+"F7.wireOp",EDGE,"E67")])]})]});
            fillet(context, id + "F14", {"entities" : qUnion([Q0, Q1, Q2, Q3, Q4, Q5]), "radius" : 3 * mm, "tangentPropagation" : true, "allowEdgeOverflow" : false});
        }
        {
            var Q0;
            Q0=makeQuery(id+"F1.opExtrude","CAP_EDGE",EDGE,{"disambiguationData":[OSD([sQuery(id+"F0.wireOp",EDGE,"E1.bottom")])],"isStart":false});
            fillet(context, id + "F15", {"entities" : qUnion([Q0]), "radius" : 2 * mm, "tangentPropagation" : true, "allowEdgeOverflow" : false});
        }
        {
            var Q0;
            {var subQ0=sQuery(id+"F0.wireOp",EDGE,"E21.filletArc");var subQ1=sQuery(id+"F0.wireOp",EDGE,"E7");var subQ2=sQuery(id+"F0.wireOp",EDGE,"E6");var subQ3=sQuery(id+"F0.wireOp",EDGE,"E5");var subQ4=sQuery(id+"F0.wireOp",EDGE,"E4");var subQ5=sQuery(id+"F0.wireOp",EDGE,"E22.filletArc");var subQ6=sQuery(id+"F0.wireOp",EDGE,"E1.bottom");var subQ7=sQuery(id+"F0.wireOp",EDGE,"E1.right");var subQ8=sQuery(id+"F0.wireOp",EDGE,"E1.top");var subQ9=sQuery(id+"F0.wireOp",EDGE,"E1.left");var subQ10=sQuery(id+"F0.wireOp",EDGE,"E23.filletArc");var subQ11=sQuery(id+"F0.wireOp",EDGE,"E24.filletArc");Q0=makeQuery(id+"F2.boolean.opBoolean","SPLIT",FACE,{"disambiguationData":[TD([makeQuery(id+"F1.opExtrude","SWEPT_FACE",FACE,{"disambiguationData":[OSD([subQ6])]})])],"derivedFrom":makeQuery(id+"F1.opExtrude","CAP_FACE",FACE,{"disambiguationData":[OSD([subQ6,subQ8,subQ9,subQ7,subQ4,subQ3,subQ2,subQ1,subQ0,subQ5,subQ10,subQ11])],"isStart":true})});}
            var sketch = newSketch(context, id + "F16", { "sketchPlane" : qUnion([Q0])});
            skLineSegment(sketch, "E79", {"start": v(0, 90) * mm, "end": v(0, 120) * mm, "construction": true});
            skCircle(sketch, "E80", {"center": v(0, 120) * mm, "radius": 6 * mm});
            skArc(sketch, "E81", {"start": v(15, 120) * mm, "mid": v(0, 135) * mm, "end": v(-15, 120) * mm});
            skLineSegment(sketch, "E82", {"start": v(-15, 120) * mm, "end": v(-15, 108) * mm});
            skLineSegment(sketch, "E83", {"start": v(15, 120) * mm, "end": v(15, 108) * mm});
            skLineSegment(sketch, "E84", {"start": v(15, 108) * mm, "end": v(33, 90) * mm});
            skLineSegment(sketch, "E85", {"start": v(-15, 108) * mm, "end": v(-33, 90) * mm});
            skLineSegment(sketch, "E86", {"start": v(-80, 0) * mm, "end": v(80, 0) * mm, "construction": true});
            skLineSegment(sketch, "E87.MirrorCS", {"start": v(0, -90) * mm, "end": v(0, -120) * mm, "construction": true});
            skCircle(sketch, "E88.MirrorC", {"center": v(0, -120) * mm, "radius": 6 * mm});
            skLineSegment(sketch, "E89.MirrorCS", {"start": v(15, -108) * mm, "end": v(33, -90) * mm});
            skLineSegment(sketch, "E90.MirrorCS", {"start": v(15, -120) * mm, "end": v(15, -108) * mm});
            skLineSegment(sketch, "E91.MirrorCS", {"start": v(-15, -120) * mm, "end": v(-15, -108) * mm});
            skLineSegment(sketch, "E92.MirrorCS", {"start": v(-15, -108) * mm, "end": v(-33, -90) * mm});
            skArc(sketch, "E93.MirrorCS", {"start": v(15, -120) * mm, "mid": v(0, -135) * mm, "end": v(-15, -120) * mm});
            skSolve(sketch);
        }
        {
            var Q0;
            Q0=makeQuery(id+"F16.imprint","IMPRINT",FACE,{"disambiguationData":[TD([[makeQuery(id+"F16.imprint","IMPRINT",EDGE,{"derivedFrom":makeQuery(id+"F1.opExtrude","CAP_EDGE",EDGE,{"disambiguationData":[OSD([sQuery(id+"F0.wireOp",EDGE,"E1.left")])],"isStart":true})}),-1.0]])]});
            var Q1;
            Q1=makeQuery(id+"F16.imprint","IMPRINT",FACE,{"disambiguationData":[TD([[makeQuery(id+"F16.imprint","IMPRINT",EDGE,{"derivedFrom":sQuery(id+"F16.wireOp",EDGE,"E80")}),-1.0]])]});
            var Q2;
            Q2=makeQuery(id+"F16.imprint","IMPRINT",FACE,{"disambiguationData":[TD([[makeQuery(id+"F16.imprint","IMPRINT",EDGE,{"derivedFrom":sQuery(id+"F16.wireOp",EDGE,"E88.MirrorC")}),1.0]])]});
            var Q3;
            Q3=makeQuery(id+"F2.opExtrude","CAP_FACE",FACE,{"disambiguationData":[OSD([sQuery(id+"F0.wireOp",EDGE,"E12"),sQuery(id+"F0.wireOp",EDGE,"E13"),sQuery(id+"F0.wireOp",EDGE,"E14"),sQuery(id+"F0.wireOp",EDGE,"E15"),sQuery(id+"F0.wireOp",EDGE,"E17.filletArc"),sQuery(id+"F0.wireOp",EDGE,"E18.filletArc"),sQuery(id+"F0.wireOp",EDGE,"E19.filletArc"),sQuery(id+"F0.wireOp",EDGE,"E20.filletArc"),sQuery(id+"F0.wireOp",EDGE,"E25.0"),sQuery(id+"F0.wireOp",EDGE,"E25.1"),sQuery(id+"F0.wireOp",EDGE,"E25.2"),sQuery(id+"F0.wireOp",EDGE,"E25.3"),sQuery(id+"F0.wireOp",EDGE,"E25.4"),sQuery(id+"F0.wireOp",EDGE,"E25.5"),sQuery(id+"F0.wireOp",EDGE,"E25.6"),sQuery(id+"F0.wireOp",EDGE,"E25.7")])],"isStart":false});
            extrude(context, id + "F17", {"entities" : qUnion([Q0, Q1, Q2]), "endBound" : BoundingType.UP_TO_SURFACE, "depth" : 25 * mm, "endBoundEntityFace" : qUnion([Q3]), "offsetDistance" : 25 * mm});
        }
    });
